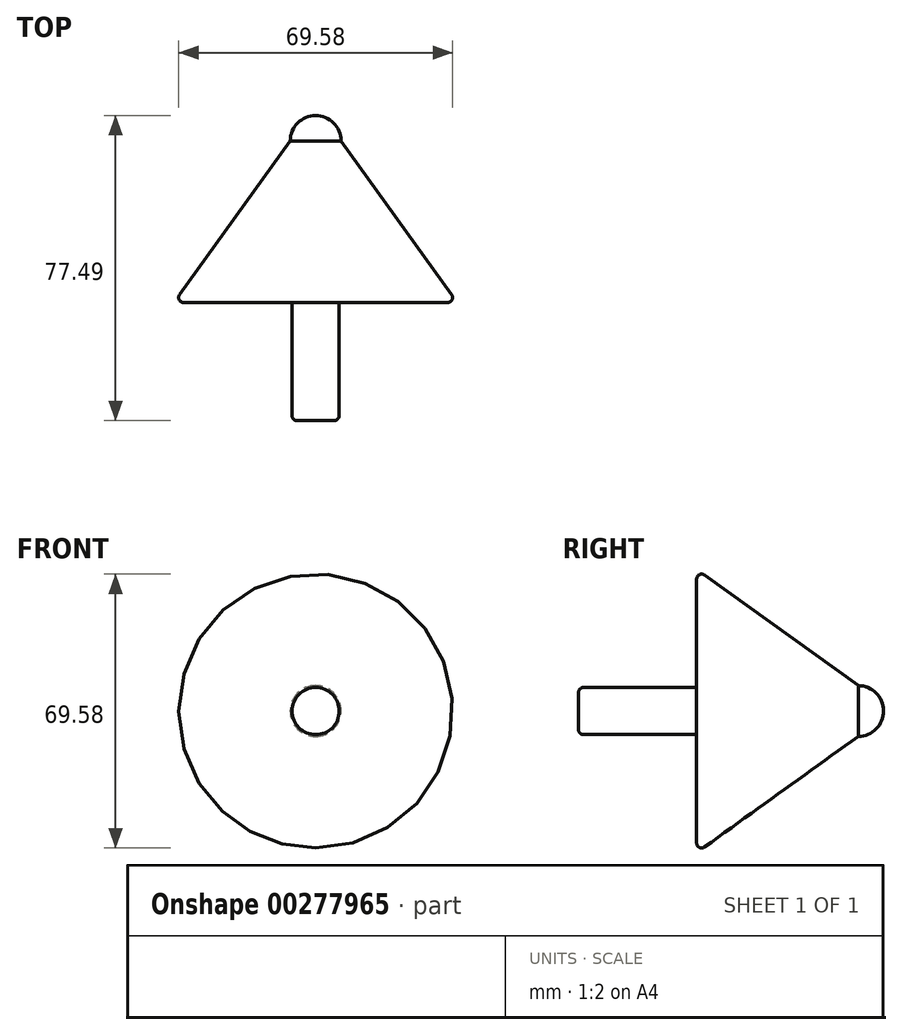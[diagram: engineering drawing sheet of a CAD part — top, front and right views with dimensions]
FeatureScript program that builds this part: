
annotation { "Feature Type Name" : "Feature", "Feature Type Description" : "" }
export const myFeature = defineFeature(function(context is Context, id is Id, definition is map)
    precondition{}
    {
        {
            var Q0;
            Q0=qCreatedBy(makeId("Right.planeOp"),FACE);
            var sketch = newSketch(context, id + "F0", { "sketchPlane" : qUnion([Q0])});
            skLineSegment(sketch, "E0", {"start": v(0, 0) * mm, "end": v(80, 0) * mm, "construction": true});
            skLineSegment(sketch, "E1", {"start": v(0, 0) * mm, "end": v(0, 4.73) * mm});
            skLineSegment(sketch, "E2", {"start": v(1.27, 6) * mm, "end": v(30, 6) * mm});
            skLineSegment(sketch, "E3", {"start": v(30, 6) * mm, "end": v(30, 33.52) * mm});
            skLineSegment(sketch, "E4", {"start": v(32.01, 34.55) * mm, "end": v(71.05, 6.45) * mm});
            skLineSegment(sketch, "E5", {"start": v(71.05, 0) * mm, "end": v(71.05, 6.45) * mm, "construction": true});
            skArc(sketch, "E6", {"start": v(71.05, 6.45) * mm, "mid": v(75.6, 4.56) * mm, "end": v(77.5, 0) * mm});
            skPoint(sketch, "E7.visualSharp", {"position": v(30, 36) * mm});
            skArc(sketch, "E7.filletArc", {"start": v(32.01, 34.55) * mm, "mid": v(30.7, 34.65) * mm, "end": v(30, 33.52) * mm});
            skLineSegment(sketch, "E8", {"start": v(0, 0) * mm, "end": v(77.5, 0) * mm});
            skPoint(sketch, "E9.visualSharp", {"position": v(0, 6) * mm});
            skArc(sketch, "E9.filletArc", {"start": v(1.27, 6) * mm, "mid": v(0.37, 5.63) * mm, "end": v(0, 4.73) * mm});
            skSolve(sketch);
        }
        {
            var Q0;
            Q0=makeQuery(id+"F0.imprint","IMPRINT",FACE,{"disambiguationData":[TD([[makeQuery(id+"F0.imprint","IMPRINT",EDGE,{"derivedFrom":sQuery(id+"F0.wireOp",EDGE,"E1")}),-1.0]])]});
            var Q1;
            Q1=sQuery(id+"F0.wireOp",EDGE,"E8");
            revolve(context, id + "F1", {"entities" : qUnion([Q0]), "axis" : qUnion([Q1]), "revolveType" : RevolveType.FULL});
        }
    });
